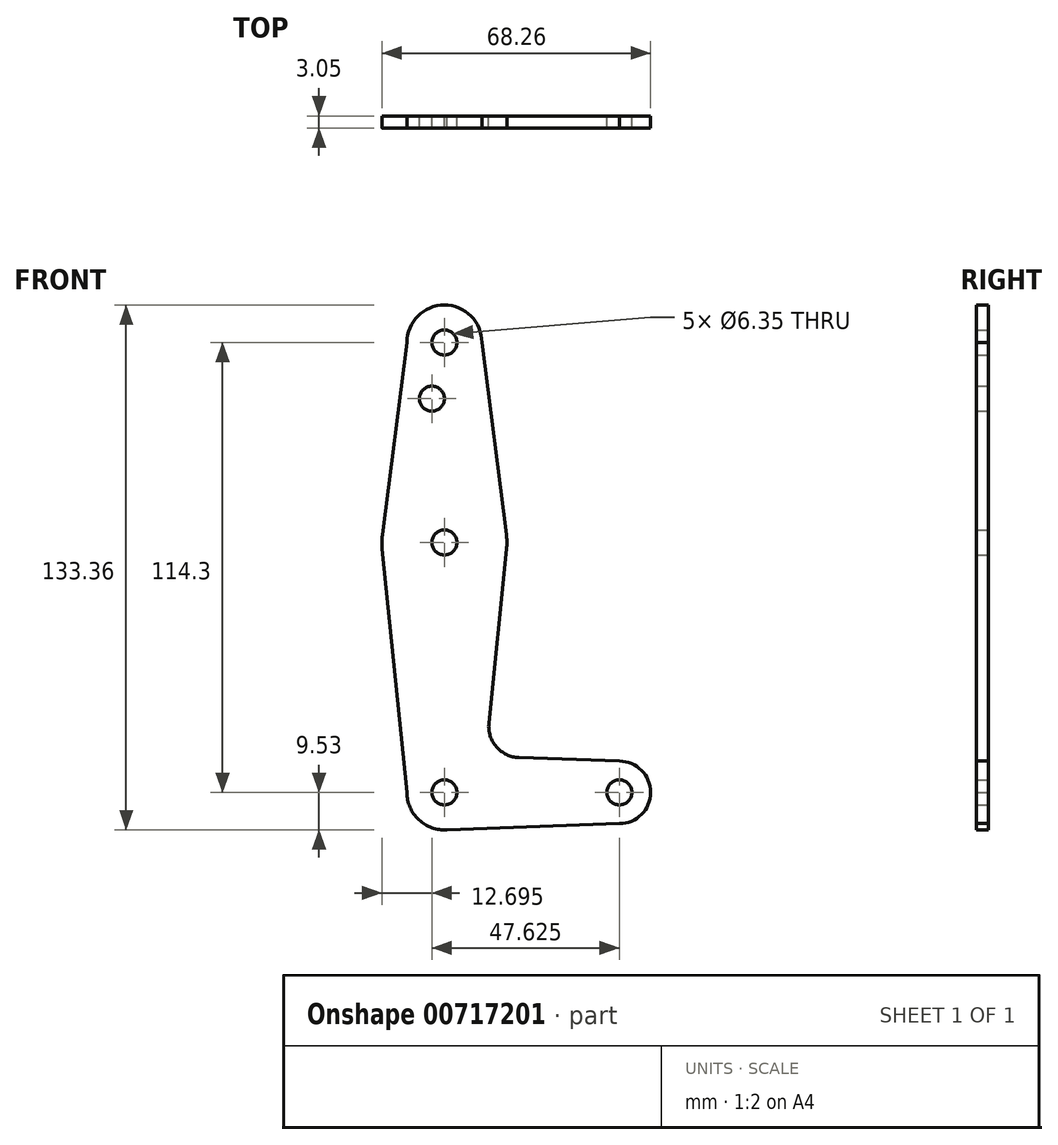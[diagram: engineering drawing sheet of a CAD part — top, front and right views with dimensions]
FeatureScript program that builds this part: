
annotation { "Feature Type Name" : "Feature", "Feature Type Description" : "" }
export const myFeature = defineFeature(function(context is Context, id is Id, definition is map)
    precondition{}
    {
        {
            var Q0;
            Q0=qCreatedBy(makeId("Front.planeOp"),FACE);
            var sketch = newSketch(context, id + "F0", { "sketchPlane" : qUnion([Q0])});
            skLineSegment(sketch, "E0", {"start": v(0, 0) * mm, "end": v(0, 114.3) * mm, "construction": true});
            skLineSegment(sketch, "E1", {"start": v(0, 0) * mm, "end": v(44.45, 0) * mm, "construction": true});
            skCircle(sketch, "E2", {"center": v(0, 114.3) * mm, "radius": 9.53 * mm});
            skCircle(sketch, "E3", {"center": v(0, 63.5) * mm, "radius": 15.88 * mm});
            skCircle(sketch, "E4", {"center": v(0, 0) * mm, "radius": 9.53 * mm});
            skCircle(sketch, "E5", {"center": v(44.45, 0) * mm, "radius": 7.94 * mm});
            skLineSegment(sketch, "E6", {"start": v(18.93, 8.85) * mm, "end": v(44.45, 7.94) * mm});
            skLineSegment(sketch, "E7", {"start": v(0, -9.52) * mm, "end": v(44.45, -7.94) * mm});
            skLineSegment(sketch, "E8", {"start": v(-9.53, 114.3) * mm, "end": v(-15.75, 65.5) * mm});
            skLineSegment(sketch, "E9", {"start": v(-15.8, 61.9) * mm, "end": v(-9.52, 0) * mm});
            skLineSegment(sketch, "E10", {"start": v(15.75, 65.5) * mm, "end": v(9.53, 114.3) * mm});
            skLineSegment(sketch, "E11", {"start": v(15.8, 61.9) * mm, "end": v(11.3, 17.6) * mm});
            skCircle(sketch, "E12", {"center": v(0, 114.3) * mm, "radius": 3.18 * mm});
            skCircle(sketch, "E13", {"center": v(0, 63.5) * mm, "radius": 3.18 * mm});
            skCircle(sketch, "E14", {"center": v(0, 0) * mm, "radius": 3.18 * mm});
            skCircle(sketch, "E15", {"center": v(44.45, 0) * mm, "radius": 3.18 * mm});
            skCircle(sketch, "E16", {"center": v(-3.18, 100.03) * mm, "radius": 3.18 * mm});
            skArc(sketch, "E17.filletArc", {"start": v(11.3, 17.6) * mm, "mid": v(13.22, 11.57) * mm, "end": v(18.93, 8.85) * mm});
            skSolve(sketch);
        }
        {
            var Q0;
            Q0 = qSketchRegion(id + "F0", true);
            extrude(context, id + "F1", {"entities" : qUnion([Q0]), "depth" : 3.05 * mm, "offsetDistance" : 25.4 * mm});
        }
    });
